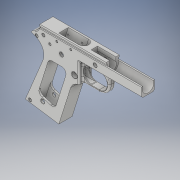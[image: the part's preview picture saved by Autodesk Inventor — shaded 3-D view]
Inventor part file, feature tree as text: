
AUTODESK INVENTOR PART (.ipt)
format: ipt  version: 2018.3 (Build 223284000, 284)  size: 657,920 bytes
history: native  units: in
note: dims shown in document units (in); Inventor stores cm internally (conversion verified against a paired STEP export)
features: extrude x10, sketch x9, plane x5, fillet x2, chamfer x1
ambient origin geometry x8: Origin, YZ Plane, XZ Plane, XY Plane, X Axis, Y Axis, Z Axis, Center Point
bodies: Solid1 (feature_tree)
feature tree (27):
  sketch  "Sketch1"  dims[d0=0.03in d1=0.849in]
  extrude  "Extrusion1"  Depth=0.849in
  chamfer  "Chamfer1"  Distance=2.88in
  plane  "Work Plane1"
  sketch  "Sketch2"  dims[d2=0.424in]
  extrude  "Extrusion2"  Depth=0.233in
  sketch  "Sketch3"  dims[d3=2.66in]
  plane  "Work Plane2"
  extrude  "Extrusion3"  Depth=0.233in
  extrude  "Extrusion4"  Depth=0.233in
  fillet  "Fillet1"  Radius=0.5in
  fillet  "Fillet2"  Radius=1.031in
  plane  "Work Plane3"
  extrude  "Extrusion5"  Depth=0.233in
  extrude  "Extrusion6"  Depth=0.233in
  plane  "Work Plane4"
  extrude  "Extrusion7"  Depth=0.233in
  sketch  "Sketch9"  dims[d9=0.1202in]
  extrude  "Extrusion8"  Depth=0.233in
  extrude  "Extrusion9"  Depth=0.233in
  plane  "Work Plane6"
  extrude  "Extrusion10"  TaperAngle=22.5deg  [1 undecoded]
  sketch  "Sketch4"  dims[d4=0.59in]
  sketch  "Sketch6"  dims[d6=0.44in]
  sketch  "Sketch8"  dims[d7=0.924in]
  sketch  "Sketch12"  dims[d10=1.28in]
  sketch  "Sketch13"  dims[d11=3.03in d12=2.88in d13=0.5in d14=0.5in d15=0.5in d16=0.5in d17=1.031in d18=0.26in d19=0.0577in d20=0.795in d21=0.138in d22=0.21in d23=22.5deg d24=0.924in d26=0.56in d27=0.75in d28=1.229in d29=0.016in d30=0.1567in d31=0.905in d32=0.345in d33=0.5944in d34=0.27in d35=0.47in d36=0.565in d37=0.29in d39=0.45in d40=0.32in d41=3.745in d42=0.157in d43=0.201in d44=0.2179in d45=3.018in d46=3.309in d47=3.595in d48=0.313in d49=1.095in d50=1.193in d51=0.2179in d52=1.937in d53=0.431in d54=0.0988in d55=0.0988in d56=0.8016in d57=1.402in d58=0.076in d59=0.0625in d60=2.328in d61=0.307in d62=0.1575in d63=2.973in d64=0.1558in d65=3.368in d66=0.21in d67=0.11in d68=2.602in d69=0.252in d70=0.762in d71=0.0in d72=0.015in d73=0.125in d74=0.0016in d75=0.0in d76=0.751in d77=0.1in d78=0.314in d79=0.314in d80=0.119in d81=0.449in d82=0.45in d83=0.089in d84=0.762in d85=0.0in d86=0.82in d87=0.658in d97=0.658in d98=0.631in d99=3.0in d100=0.0in d101=0.089in d102=1.0in d103=0.1835in d104=0.1835in d105=3.5745in d106=0.0in d107=0.1in d109=0.02in d110=0.08in d113=0.551in d114=1.106in d115=1.0in d116=0.0in d117=1.0in d118=0.431in d119=0.0in d120=0.0in d121=0.089in d122=0.449in d123=0.365in d124=1.0in d125=0.0in d127=0.25in d128=0.0in d132=2.526in d133=0.484in d134=0.215in d135=6.75in d136=0.0in d137=-0.878in d138=0.321in d139=0.27in d140=0.233in d141=0.0in]
note: 1 required parameter value undecoded (feature->parameter linkage not recoverable at this tier; creation-order binding heuristic only, values carry confidence <= 0.55)
